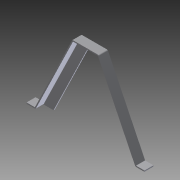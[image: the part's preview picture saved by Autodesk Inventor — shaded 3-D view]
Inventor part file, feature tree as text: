
AUTODESK INVENTOR PART (.ipt)
format: ipt  version: 2012 (Build 160160000, 160)  size: 131,584 bytes
history: native  units: in
note: dims shown in document units (in); Inventor stores cm internally (conversion verified against a paired STEP export)
features: extrude x2, fillet x2, sketch x1
ambient origin geometry x8: Origin, YZ Plane, XZ Plane, XY Plane, X Axis, Y Axis, Z Axis, Center Point
bodies: Solid1 (feature_tree)
feature tree (5):
  sketch  "Sketch1"  dims[d1=2.75in d4=0.125in d5=0.125in d10=1.0in d11=0.0in d12=0.125in d13=0.0in d14=0.0312in d15=0.125in d29=0.4013in d34=1.0in d35=1.0in d36=0.0625in d37=0.0625in d41=0.125in d43=8.625in d44=0.125in d45=0.4405in d46=0.4405in d47=0.125in d48=1.0in d49=1.0in d50=13.0in]
  extrude  "Extrusion1"  Depth=0.125in
  extrude  "Extrusion2"  Depth=0.125in
  fillet  "Fillet1"  Radius=1.0in
  fillet  "Fillet2"  Radius=0.125in
